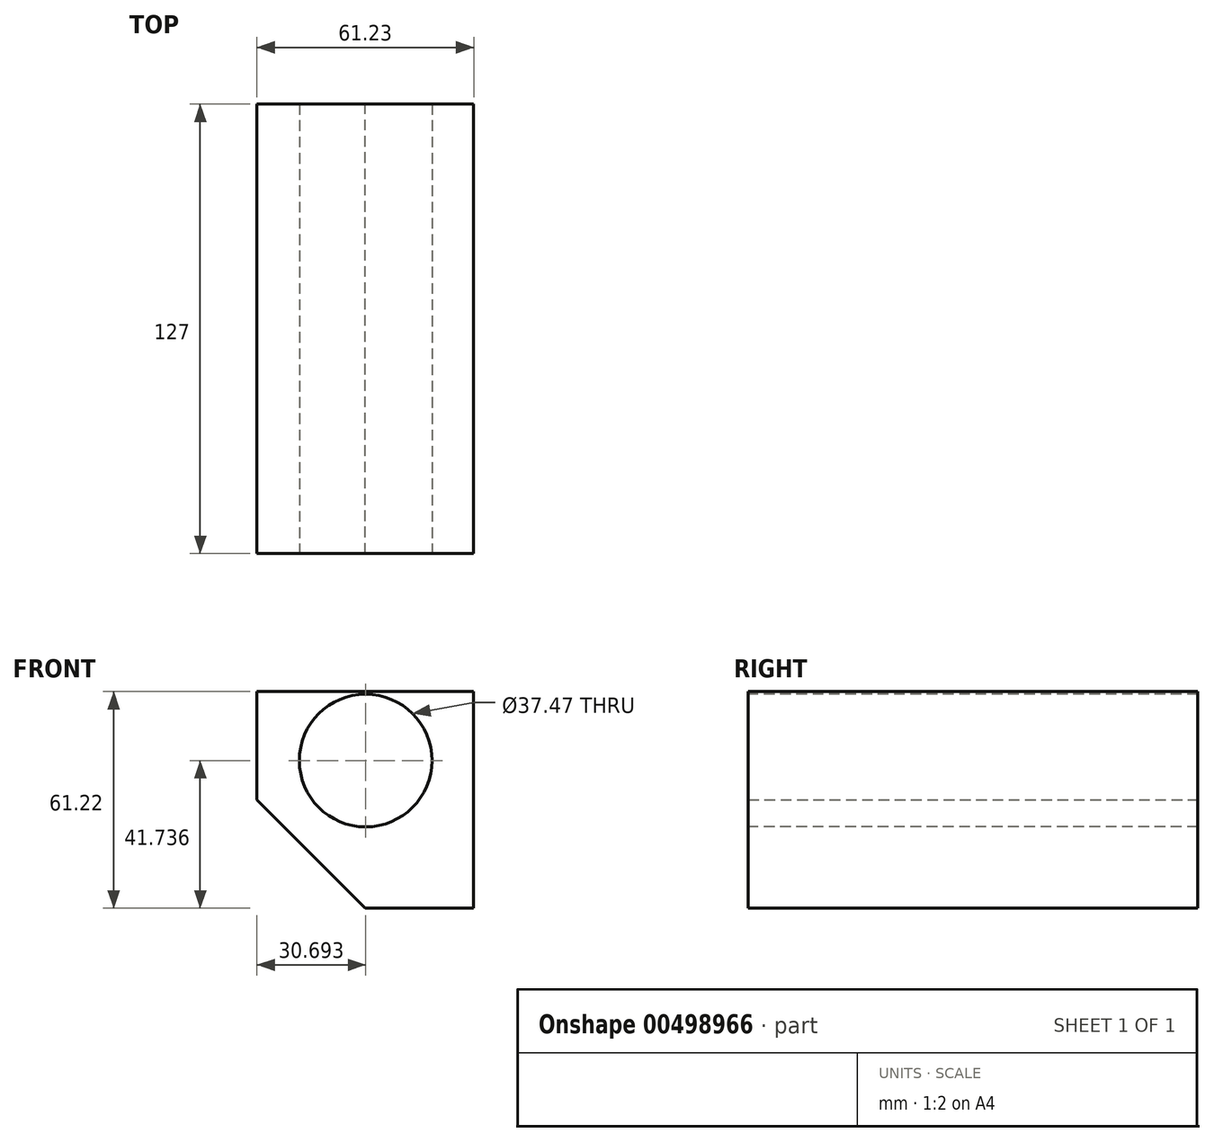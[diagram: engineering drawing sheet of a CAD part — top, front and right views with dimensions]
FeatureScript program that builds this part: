
annotation { "Feature Type Name" : "Feature", "Feature Type Description" : "" }
export const myFeature = defineFeature(function(context is Context, id is Id, definition is map)
    precondition{}
    {
        {
            var Q0;
            Q0=qCreatedBy(makeId("Front.planeOp"),FACE);
            var sketch = newSketch(context, id + "F0", { "sketchPlane" : qUnion([Q0])});
            skLineSegment(sketch, "E0", {"start": v(-44.8, 39.94) * mm, "end": v(-44.8, -21.28) * mm});
            skLineSegment(sketch, "E1", {"start": v(16.43, -21.28) * mm, "end": v(16.43, 39.94) * mm});
            skLineSegment(sketch, "E2", {"start": v(16.43, 39.94) * mm, "end": v(-44.8, 39.94) * mm});
            skLineSegment(sketch, "E3", {"start": v(-44.8, -21.28) * mm, "end": v(16.43, -21.28) * mm});
            skSolve(sketch);
        }
        {
            var Q0;
            Q0 = qSketchRegion(id + "F0", true);
            extrude(context, id + "F1", {"entities" : qUnion([Q0]), "depth" : 127 * mm, "offsetDistance" : 25.4 * mm});
        }
        {
            var Q0;
            Q0=makeQuery(id+"F1.opExtrude","CAP_FACE",FACE,{"disambiguationData":[OSD([sQuery(id+"F0.wireOp",EDGE,"E0"),sQuery(id+"F0.wireOp",EDGE,"E1"),sQuery(id+"F0.wireOp",EDGE,"E2"),sQuery(id+"F0.wireOp",EDGE,"E3")])],"isStart":false});
            var sketch = newSketch(context, id + "F2", { "sketchPlane" : qUnion([Q0])});
            skCircle(sketch, "E4", {"center": v(-14.1, 20.46) * mm, "radius": 18.74 * mm});
            skSolve(sketch);
        }
        {
            var Q0;
            Q0=makeQuery(id+"F2.imprint","IMPRINT",FACE,{"disambiguationData":[TD([[makeQuery(id+"F2.imprint","IMPRINT",EDGE,{"derivedFrom":sQuery(id+"F2.wireOp",EDGE,"E4")}),1.0]])]});
            extrude(context, id + "F3", {"entities" : qUnion([Q0]), "operationType" : NewBodyOperationType.REMOVE, "endBound" : BoundingType.THROUGH_ALL, "oppositeDirection" : true, "depth" : 25.4 * mm, "offsetDistance" : 25.4 * mm});
        }
        {
            var Q0;
            Q0=makeQuery(id+"F1.opExtrude","CAP_FACE",FACE,{"disambiguationData":[OSD([sQuery(id+"F0.wireOp",EDGE,"E0"),sQuery(id+"F0.wireOp",EDGE,"E1"),sQuery(id+"F0.wireOp",EDGE,"E2"),sQuery(id+"F0.wireOp",EDGE,"E3")])],"isStart":true});
            var sketch = newSketch(context, id + "F4", { "sketchPlane" : qUnion([Q0])});
            skLineSegment(sketch, "E5", {"start": v(14.19, -21.28) * mm, "end": v(-16.43, 9.33) * mm});
            skLineSegment(sketch, "E6", {"start": v(-16.43, 9.33) * mm, "end": v(14.19, -21.28) * mm});
            skLineSegment(sketch, "E7", {"start": v(14.19, -21.28) * mm, "end": v(44.8, 9.33) * mm});
            skSolve(sketch);
        }
        {
            var Q0;
            {var subQ0=sQuery(id+"F4.wireOp",EDGE,"E6");Q0=makeQuery(id+"F4.imprint","IMPRINT",FACE,{"disambiguationData":[TD([[makeQuery(id+"F4.imprint","IMPRINT",EDGE,{"derivedFrom":subQ0}),-1.0]])]});}
            var Q1;
            {var subQ0=sQuery(id+"F4.wireOp",EDGE,"E7");Q1=makeQuery(id+"F4.imprint","IMPRINT",FACE,{"disambiguationData":[TD([[makeQuery(id+"F4.imprint","IMPRINT",EDGE,{"derivedFrom":subQ0}),-1.0]])]});}
            extrude(context, id + "F5", {"entities" : qUnion([Q0, Q1]), "operationType" : NewBodyOperationType.REMOVE, "endBound" : BoundingType.THROUGH_ALL, "oppositeDirection" : true, "depth" : 25.4 * mm, "offsetDistance" : 25.4 * mm});
        }
    });
